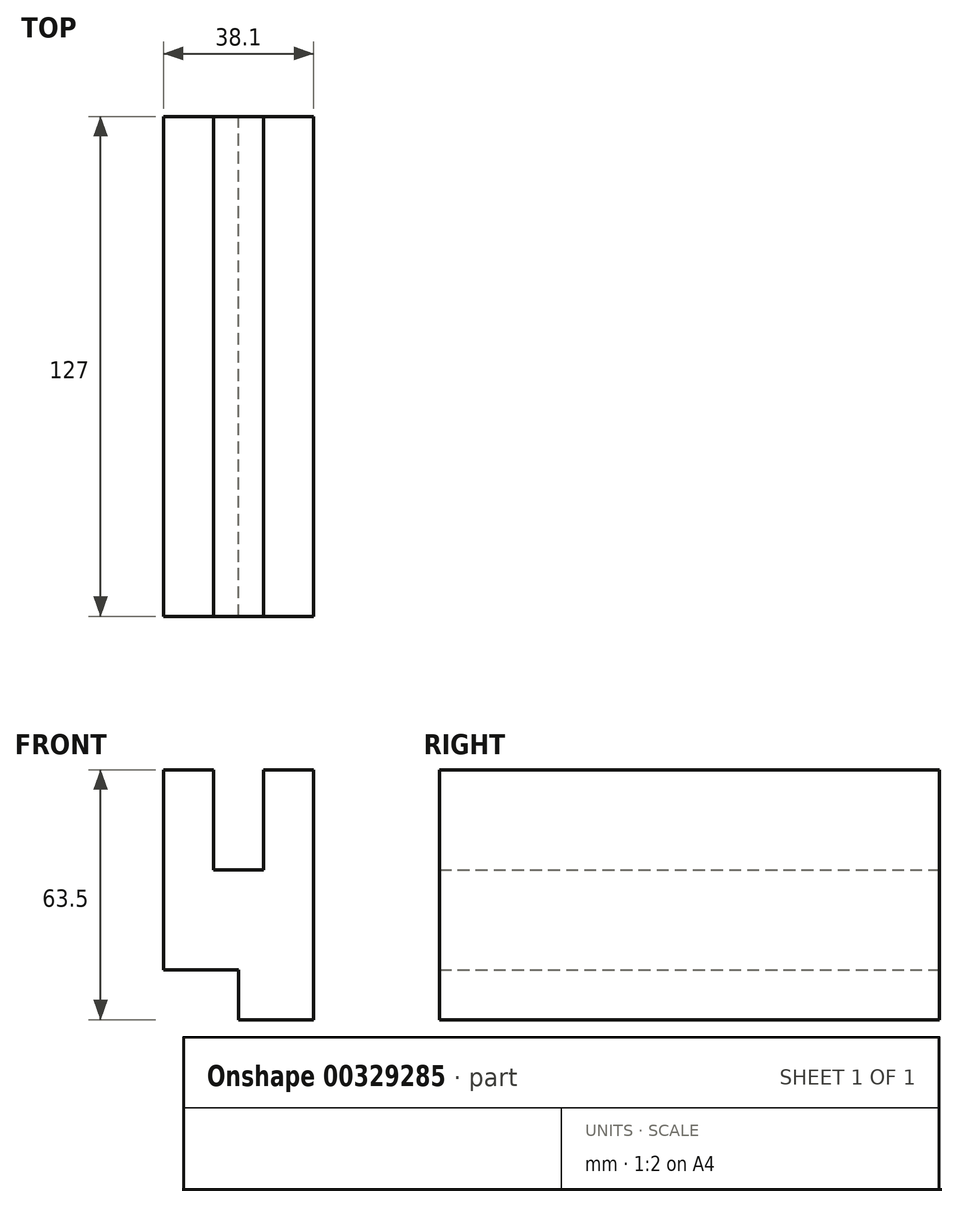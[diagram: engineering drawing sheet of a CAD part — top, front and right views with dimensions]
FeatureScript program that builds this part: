
annotation { "Feature Type Name" : "Feature", "Feature Type Description" : "" }
export const myFeature = defineFeature(function(context is Context, id is Id, definition is map)
    precondition{}
    {
        {
            var Q0;
            Q0=qCreatedBy(makeId("Front.planeOp"),FACE);
            var sketch = newSketch(context, id + "F0", { "sketchPlane" : qUnion([Q0])});
            skLineSegment(sketch, "E0", {"start": v(44.78, -20.24) * mm, "end": v(44.78, 43.26) * mm});
            skLineSegment(sketch, "E1", {"start": v(44.78, 43.26) * mm, "end": v(32.08, 43.26) * mm});
            skLineSegment(sketch, "E2", {"start": v(32.08, 43.26) * mm, "end": v(32.08, 17.86) * mm});
            skLineSegment(sketch, "E3", {"start": v(32.08, 17.86) * mm, "end": v(19.38, 17.86) * mm});
            skLineSegment(sketch, "E4", {"start": v(19.38, 17.86) * mm, "end": v(19.38, 43.26) * mm});
            skLineSegment(sketch, "E5", {"start": v(19.38, 43.26) * mm, "end": v(6.68, 43.26) * mm});
            skPoint(sketch, "E5.endSnap0", {"position": v(38.43, 43.26) * mm});
            skLineSegment(sketch, "E6", {"start": v(44.78, -20.24) * mm, "end": v(25.73, -20.24) * mm});
            skLineSegment(sketch, "E7", {"start": v(25.73, -20.24) * mm, "end": v(25.73, -7.54) * mm});
            skLineSegment(sketch, "E8", {"start": v(25.73, -7.54) * mm, "end": v(6.68, -7.54) * mm});
            skLineSegment(sketch, "E9", {"start": v(6.68, -7.54) * mm, "end": v(6.68, 43.26) * mm});
            skSolve(sketch);
        }
        {
            var Q0;
            Q0 = qSketchRegion(id + "F0", true);
            extrude(context, id + "F1", {"entities" : qUnion([Q0]), "depth" : 127 * mm});
        }
    });
